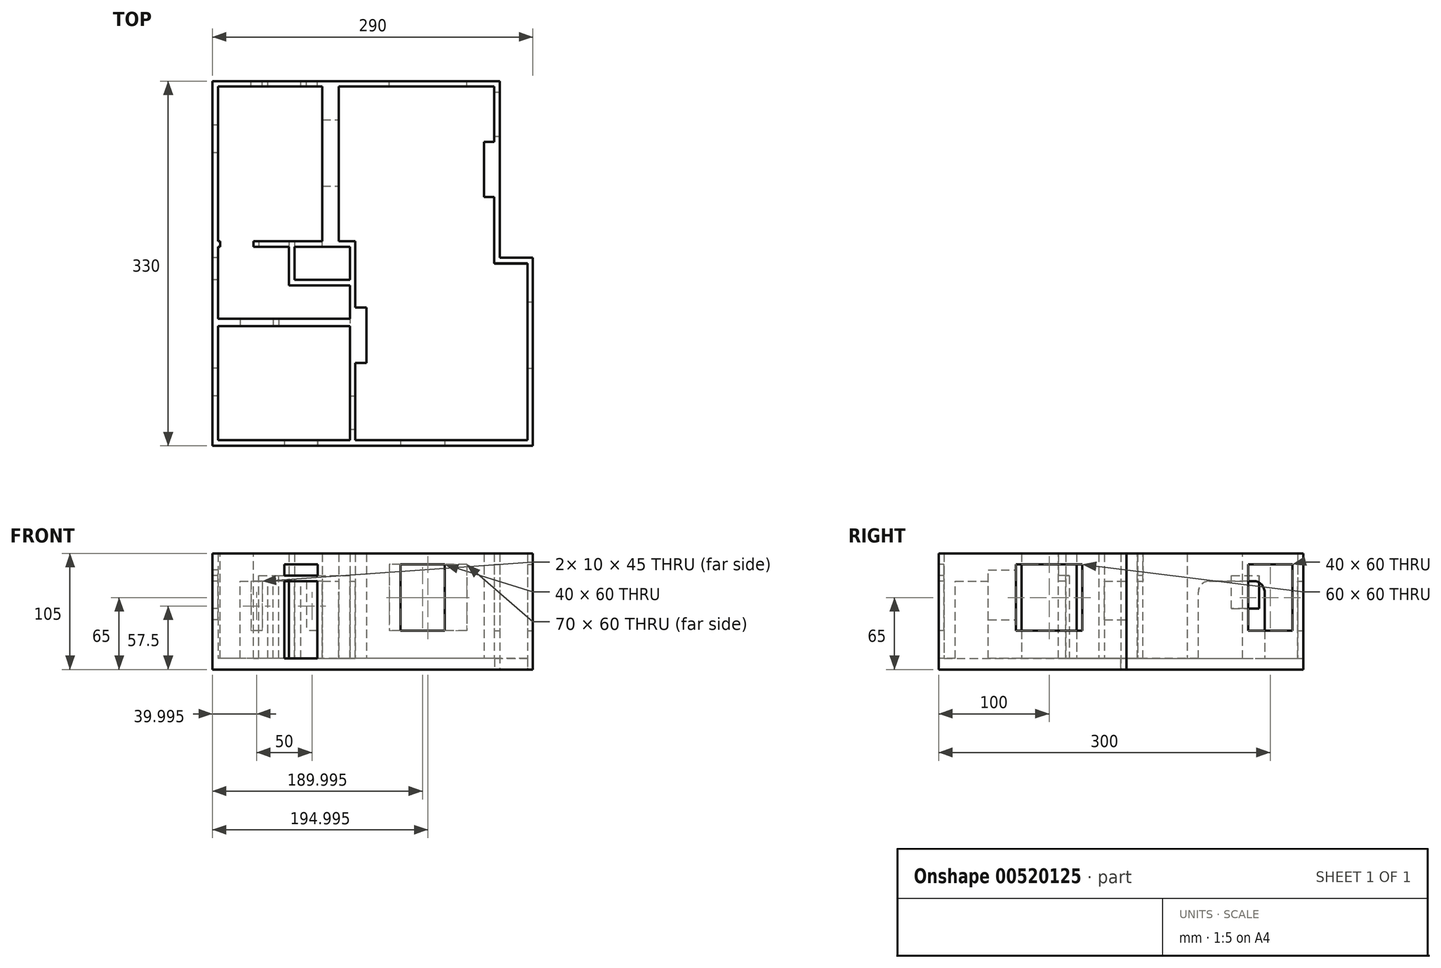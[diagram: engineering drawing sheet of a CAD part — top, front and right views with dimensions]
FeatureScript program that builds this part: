
annotation { "Feature Type Name" : "Feature", "Feature Type Description" : "" }
export const myFeature = defineFeature(function(context is Context, id is Id, definition is map)
    precondition{}
    {
        {
            var Q0;
            Q0=qCreatedBy(makeId("Top.planeOp"),FACE);
            var sketch = newSketch(context, id + "F0", { "sketchPlane" : qUnion([Q0])});
            skLineSegment(sketch, "E0.bottom", {"start": v(-137.2, 155) * mm, "end": v(112.8, 155) * mm});
            skLineSegment(sketch, "E0.top", {"start": v(-137.2, -165) * mm, "end": v(142.8, -165) * mm});
            skLineSegment(sketch, "E0.left", {"start": v(-137.2, 155) * mm, "end": v(-137.2, -165) * mm});
            skLineSegment(sketch, "E0.right", {"start": v(142.8, -5) * mm, "end": v(142.8, -165) * mm});
            skLineSegment(sketch, "E1", {"start": v(112.8, 155) * mm, "end": v(112.8, -5) * mm});
            skLineSegment(sketch, "E2", {"start": v(112.8, -5) * mm, "end": v(142.8, -5) * mm});
            skLineSegment(sketch, "E3.right", {"start": v(112.8, 61.59) * mm, "end": v(112.8, 0.5) * mm});
            skLineSegment(sketch, "E4", {"start": v(117.8, 0) * mm, "end": v(147.8, 0) * mm});
            skLineSegment(sketch, "E5", {"start": v(147.8, 0) * mm, "end": v(147.8, -170) * mm});
            skLineSegment(sketch, "E6", {"start": v(147.8, -170) * mm, "end": v(-142.2, -170) * mm});
            skLineSegment(sketch, "E7", {"start": v(-142.2, -170) * mm, "end": v(-142.2, 160) * mm});
            skLineSegment(sketch, "E8", {"start": v(-142.2, 160) * mm, "end": v(117.8, 160) * mm});
            skLineSegment(sketch, "E9", {"start": v(117.8, 0) * mm, "end": v(117.8, 160) * mm});
            skSolve(sketch);
        }
        {
            var Q0;
            Q0=qCreatedBy(makeId("Top.planeOp"),FACE);
            var sketch = newSketch(context, id + "F1", { "sketchPlane" : qUnion([Q0])});
            skLineSegment(sketch, "E10", {"start": v(-137.23, -165.92) * mm, "end": v(-137.39, 155.26) * mm});
            skLineSegment(sketch, "E11", {"start": v(-137.39, 155.26) * mm, "end": v(113.01, 155.38) * mm});
            skLineSegment(sketch, "E12", {"start": v(144.03, -5.33) * mm, "end": v(143.4, -165.3) * mm});
            skLineSegment(sketch, "E13", {"start": v(143.4, -165.3) * mm, "end": v(-137.23, -165.92) * mm});
            skLineSegment(sketch, "E14", {"start": v(113.01, -5.33) * mm, "end": v(144.03, -5.33) * mm});
            skLineSegment(sketch, "E15", {"start": v(113.01, 155.38) * mm, "end": v(113.01, -5.33) * mm});
            skSolve(sketch);
        }
        {
            var Q0;
            Q0 = qSketchRegion(id + "F1", true);
            extrude(context, id + "F2", {"entities" : qUnion([Q0]), "depth" : 10 * mm, "offsetDistance" : 25 * mm});
        }
        {
            var Q0;
            Q0 = qSketchRegion(id + "F0", true);
            extrude(context, id + "F3", {"entities" : qUnion([Q0]), "operationType" : NewBodyOperationType.ADD, "depth" : 105 * mm, "offsetDistance" : 25 * mm});
        }
        {
            var Q0;
            Q0=makeQuery(id+"F3.boolean.opBoolean","SPLIT",FACE,{"disambiguationData":[TD([makeQuery(id+"F3.opExtrude","SWEPT_FACE",FACE,{"disambiguationData":[OSD([sQuery(id+"F0.wireOp",EDGE,"E0.bottom")])]}),makeQuery(id+"F3.opExtrude","SWEPT_FACE",FACE,{"disambiguationData":[OSD([sQuery(id+"F0.wireOp",EDGE,"E0.top")])]}),makeQuery(id+"F3.opExtrude","SWEPT_FACE",FACE,{"disambiguationData":[OSD([sQuery(id+"F0.wireOp",EDGE,"E0.left")])]}),makeQuery(id+"F3.opExtrude","SWEPT_FACE",FACE,{"disambiguationData":[OSD([sQuery(id+"F0.wireOp",EDGE,"E0.right")])]}),makeQuery(id+"F3.opExtrude","SWEPT_FACE",FACE,{"disambiguationData":[OSD([sQuery(id+"F0.wireOp",EDGE,"E1"),sQuery(id+"F0.wireOp",EDGE,"E3.right")])]}),makeQuery(id+"F3.opExtrude","SWEPT_FACE",FACE,{"disambiguationData":[OSD([sQuery(id+"F0.wireOp",EDGE,"E2")])]})])],"derivedFrom":makeQuery(id+"F2.opExtrude","CAP_FACE",FACE,{"disambiguationData":[OSD([sQuery(id+"F1.wireOp",EDGE,"E10"),sQuery(id+"F1.wireOp",EDGE,"E11"),sQuery(id+"F1.wireOp",EDGE,"AHrGg0TC-f3ZD-vxQt-6p1O-15SQzwXil3k3"),sQuery(id+"F1.wireOp",EDGE,"61pY8PKr-3VqT-7SnW-i4XL-9i2g4O1dyYCC"),sQuery(id+"F1.wireOp",EDGE,"E12"),sQuery(id+"F1.wireOp",EDGE,"E13")])],"isStart":false})});
            var sketch = newSketch(context, id + "F4", { "sketchPlane" : qUnion([Q0])});
            skLineSegment(sketch, "E16", {"start": v(-28.01, 156.19) * mm, "end": v(-27.86, 125) * mm});
            skLineSegment(sketch, "E17", {"start": v(-27.86, 65) * mm, "end": v(-27.86, 15) * mm});
            skLineSegment(sketch, "E18", {"start": v(-42.86, 15) * mm, "end": v(-72.86, 15) * mm});
            skLineSegment(sketch, "E19", {"start": v(-72.86, 9.94) * mm, "end": v(-72.86, -15) * mm});
            skLineSegment(sketch, "E20", {"start": v(-12.86, -15) * mm, "end": v(-12.86, -45) * mm});
            skLineSegment(sketch, "E21", {"start": v(-12.86, -45) * mm, "end": v(-2.86, -45) * mm});
            skLineSegment(sketch, "E22", {"start": v(-2.86, -45) * mm, "end": v(-2.86, -95) * mm});
            skLineSegment(sketch, "E23", {"start": v(-2.86, -95) * mm, "end": v(-12.86, -95) * mm});
            skLineSegment(sketch, "E24", {"start": v(-12.86, -95) * mm, "end": v(-12.86, -166.02) * mm});
            skLineSegment(sketch, "E25", {"start": v(-27.86, 15) * mm, "end": v(-12.86, 15) * mm});
            skLineSegment(sketch, "E26", {"start": v(-12.86, 15) * mm, "end": v(-12.86, -15) * mm});
            skLineSegment(sketch, "E27", {"start": v(113.59, 55) * mm, "end": v(103.59, 55) * mm});
            skLineSegment(sketch, "E28", {"start": v(103.59, 55) * mm, "end": v(103.59, 105) * mm});
            skLineSegment(sketch, "E29", {"start": v(103.59, 105) * mm, "end": v(113.59, 105) * mm});
            skLineSegment(sketch, "E30.bottom", {"start": v(-67.86, 10) * mm, "end": v(-17.86, 10) * mm});
            skLineSegment(sketch, "E30.top", {"start": v(-67.86, -20) * mm, "end": v(-17.86, -20) * mm});
            skLineSegment(sketch, "E30.left", {"start": v(-67.86, 10) * mm, "end": v(-67.86, -20) * mm});
            skLineSegment(sketch, "E30.right", {"start": v(-17.86, 10) * mm, "end": v(-17.86, -20) * mm});
            skLineSegment(sketch, "E31", {"start": v(-17.93, -15) * mm, "end": v(-17.93, -20) * mm});
            skLineSegment(sketch, "E32", {"start": v(-17.86, -166.02) * mm, "end": v(-12.86, -166.02) * mm});
            skLineSegment(sketch, "E33", {"start": v(-42.86, 15) * mm, "end": v(-42.86, 55.12) * mm});
            skPoint(sketch, "E33.startSnap0", {"position": v(-42.86, 10) * mm});
            skLineSegment(sketch, "E34", {"start": v(-42.86, 156.12) * mm, "end": v(-42.86, 115.12) * mm});
            skLineSegment(sketch, "E35", {"start": v(113.59, 105) * mm, "end": v(113.59, 55) * mm});
            skLineSegment(sketch, "E36", {"start": v(-42.86, 115.12) * mm, "end": v(-42.86, 55.12) * mm});
            skLineSegment(sketch, "E37", {"start": v(-27.86, 125) * mm, "end": v(-27.86, 65) * mm});
            skLineSegment(sketch, "E38", {"start": v(-17.91, -55) * mm, "end": v(-139.35, -55.05) * mm});
            skLineSegment(sketch, "E39", {"start": v(-139.35, -55.05) * mm, "end": v(-139.34, -61.75) * mm});
            skLineSegment(sketch, "E40", {"start": v(-139.34, -61.75) * mm, "end": v(-17.9, -61.75) * mm});
            skLineSegment(sketch, "E41.trimOffspring", {"start": v(-17.9, -61.75) * mm, "end": v(-17.86, -166.02) * mm});
            skLineSegment(sketch, "E42", {"start": v(-72.86, -15) * mm, "end": v(-72.86, -25) * mm});
            skLineSegment(sketch, "E43", {"start": v(-72.86, -25) * mm, "end": v(-17.93, -25) * mm});
            skLineSegment(sketch, "E44.trimOffspring", {"start": v(-17.93, -25) * mm, "end": v(-17.91, -55) * mm});
            skLineSegment(sketch, "E45", {"start": v(-72.86, 15) * mm, "end": v(-139.22, 15) * mm});
            skLineSegment(sketch, "E46", {"start": v(-139.22, 15) * mm, "end": v(-139.22, 9.94) * mm});
            skLineSegment(sketch, "E47", {"start": v(-139.22, 9.94) * mm, "end": v(-72.86, 9.94) * mm});
            skLineSegment(sketch, "E48", {"start": v(-42.86, 156.12) * mm, "end": v(-28.01, 156.19) * mm});
            skPoint(sketch, "E49.orphan", {"position": v(-28.05, 165) * mm});
            skPoint(sketch, "E50.end.orphan", {"position": v(-28.05, 158.08) * mm});
            skSolve(sketch);
        }
        {
            var Q0;
            Q0 = qSketchRegion(id + "F4", true);
            extrude(context, id + "F5", {"entities" : qUnion([Q0]), "operationType" : NewBodyOperationType.ADD, "depth" : 95 * mm, "offsetDistance" : 25 * mm});
        }
        {
            var Q0;
            Q0=makeQuery(id+"F3.opExtrude","SWEPT_FACE",FACE,{"disambiguationData":[OSD([sQuery(id+"F0.wireOp",EDGE,"E5")])]});
            var sketch = newSketch(context, id + "F6", { "sketchPlane" : qUnion([Q0])});
            skLineSegment(sketch, "E51.bottom", {"start": v(-100, 95) * mm, "end": v(-40, 95) * mm});
            skLineSegment(sketch, "E51.top", {"start": v(-100, 35) * mm, "end": v(-40, 35) * mm});
            skLineSegment(sketch, "E51.left", {"start": v(-100, 95) * mm, "end": v(-100, 35) * mm});
            skLineSegment(sketch, "E51.right", {"start": v(-40, 95) * mm, "end": v(-40, 35) * mm});
            skSolve(sketch);
        }
        {
            var Q0;
            Q0=makeQuery(id+"F6.imprint","IMPRINT",FACE,{"disambiguationData":[TD([[makeQuery(id+"F6.imprint","IMPRINT",EDGE,{"derivedFrom":sQuery(id+"F6.wireOp",EDGE,"E51.bottom")}),-1.0]])]});
            extrude(context, id + "F7", {"entities" : qUnion([Q0]), "operationType" : NewBodyOperationType.REMOVE, "oppositeDirection" : true, "depth" : 10 * mm, "offsetDistance" : 25 * mm});
        }
        {
            var Q0;
            Q0=makeQuery(id+"F3.opExtrude","SWEPT_FACE",FACE,{"disambiguationData":[OSD([sQuery(id+"F0.wireOp",EDGE,"E9")])]});
            var sketch = newSketch(context, id + "F8", { "sketchPlane" : qUnion([Q0])});
            skLineSegment(sketch, "E52.bottom", {"start": v(110, 95) * mm, "end": v(150, 95) * mm});
            skLineSegment(sketch, "E52.top", {"start": v(110, 35) * mm, "end": v(150, 35) * mm});
            skLineSegment(sketch, "E52.left", {"start": v(110, 95) * mm, "end": v(110, 35) * mm});
            skLineSegment(sketch, "E52.right", {"start": v(150, 95) * mm, "end": v(150, 35) * mm});
            skSolve(sketch);
        }
        {
            var Q0;
            Q0 = qSketchRegion(id + "F8", true);
            extrude(context, id + "F9", {"entities" : qUnion([Q0]), "operationType" : NewBodyOperationType.REMOVE, "oppositeDirection" : true, "depth" : 10 * mm, "offsetDistance" : 25 * mm});
        }
        {
            var Q0;
            Q0=makeQuery(id+"F3.opExtrude","SWEPT_FACE",FACE,{"disambiguationData":[OSD([sQuery(id+"F0.wireOp",EDGE,"E8")])]});
            var sketch = newSketch(context, id + "F10", { "sketchPlane" : qUnion([Q0])});
            skLineSegment(sketch, "E53.bottom", {"start": v(-87.8, 95) * mm, "end": v(-17.8, 95) * mm});
            skLineSegment(sketch, "E53.top", {"start": v(-87.8, 35) * mm, "end": v(-17.8, 35) * mm});
            skLineSegment(sketch, "E53.left", {"start": v(-87.8, 95) * mm, "end": v(-87.8, 35) * mm});
            skLineSegment(sketch, "E53.right", {"start": v(-17.8, 95) * mm, "end": v(-17.8, 35) * mm});
            skLineSegment(sketch, "E54.bottom", {"start": v(97.2, 80) * mm, "end": v(107.2, 80) * mm});
            skLineSegment(sketch, "E54.top", {"start": v(97.2, 35) * mm, "end": v(107.2, 35) * mm});
            skLineSegment(sketch, "E54.left", {"start": v(97.2, 80) * mm, "end": v(97.2, 35) * mm});
            skLineSegment(sketch, "E54.right", {"start": v(107.2, 80) * mm, "end": v(107.2, 35) * mm});
            skLineSegment(sketch, "E55.bottom", {"start": v(47.2, 80) * mm, "end": v(57.2, 80) * mm});
            skLineSegment(sketch, "E55.top", {"start": v(47.2, 35) * mm, "end": v(57.2, 35) * mm});
            skLineSegment(sketch, "E55.left", {"start": v(47.2, 80) * mm, "end": v(47.2, 35) * mm});
            skLineSegment(sketch, "E55.right", {"start": v(57.2, 80) * mm, "end": v(57.2, 35) * mm});
            skLineSegment(sketch, "E56.bottom", {"start": v(62.2, 10) * mm, "end": v(92.2, 10) * mm});
            skLineSegment(sketch, "E56.top", {"start": v(62.2, 80) * mm, "end": v(92.2, 80) * mm});
            skLineSegment(sketch, "E56.left", {"start": v(62.2, 10) * mm, "end": v(62.2, 80) * mm});
            skLineSegment(sketch, "E56.right", {"start": v(92.2, 10) * mm, "end": v(92.2, 80) * mm});
            skSolve(sketch);
        }
        {
            var Q0;
            Q0 = qSketchRegion(id + "F10", true);
            extrude(context, id + "F11", {"entities" : qUnion([Q0]), "operationType" : NewBodyOperationType.REMOVE, "oppositeDirection" : true, "depth" : 10 * mm, "offsetDistance" : 25 * mm});
        }
        {
            var Q0;
            Q0=makeQuery(id+"F3.opExtrude","SWEPT_FACE",FACE,{"disambiguationData":[OSD([sQuery(id+"F0.wireOp",EDGE,"E7")])]});
            var sketch = newSketch(context, id + "F12", { "sketchPlane" : qUnion([Q0])});
            skLineSegment(sketch, "E57.bottom", {"start": v(-120, 85) * mm, "end": v(-95, 85) * mm});
            skLineSegment(sketch, "E57.top", {"start": v(-120, 55) * mm, "end": v(-95, 55) * mm});
            skLineSegment(sketch, "E57.left", {"start": v(-120, 85) * mm, "end": v(-120, 55) * mm});
            skLineSegment(sketch, "E57.right", {"start": v(-95, 85) * mm, "end": v(-95, 55) * mm});
            skLineSegment(sketch, "E58.bottom", {"start": v(0, 80) * mm, "end": v(20, 80) * mm});
            skLineSegment(sketch, "E58.top", {"start": v(0, 45) * mm, "end": v(20, 45) * mm});
            skLineSegment(sketch, "E58.left", {"start": v(0, 80) * mm, "end": v(0, 45) * mm});
            skLineSegment(sketch, "E58.right", {"start": v(20, 80) * mm, "end": v(20, 45) * mm});
            skLineSegment(sketch, "E59.bottom", {"start": v(100, 90) * mm, "end": v(125, 90) * mm});
            skLineSegment(sketch, "E59.top", {"start": v(100, 45) * mm, "end": v(125, 45) * mm});
            skLineSegment(sketch, "E59.left", {"start": v(100, 90) * mm, "end": v(100, 45) * mm});
            skLineSegment(sketch, "E59.right", {"start": v(125, 90) * mm, "end": v(125, 45) * mm});
            skSolve(sketch);
        }
        {
            var Q0;
            Q0 = qSketchRegion(id + "F12", true);
            extrude(context, id + "F13", {"entities" : qUnion([Q0]), "operationType" : NewBodyOperationType.REMOVE, "oppositeDirection" : true, "depth" : 25 * mm, "offsetDistance" : 25 * mm});
        }
        {
            var Q0;
            Q0=makeQuery(id+"F3.opExtrude","SWEPT_FACE",FACE,{"disambiguationData":[OSD([sQuery(id+"F0.wireOp",EDGE,"E6")])]});
            var sketch = newSketch(context, id + "F14", { "sketchPlane" : qUnion([Q0])});
            skLineSegment(sketch, "E60.bottom", {"start": v(-77.2, 10) * mm, "end": v(-47.2, 10) * mm});
            skLineSegment(sketch, "E60.top", {"start": v(-77.2, 80) * mm, "end": v(-47.2, 80) * mm});
            skLineSegment(sketch, "E60.left", {"start": v(-77.2, 10) * mm, "end": v(-77.2, 80) * mm});
            skLineSegment(sketch, "E60.right", {"start": v(-47.2, 10) * mm, "end": v(-47.2, 80) * mm});
            skLineSegment(sketch, "E61.bottom", {"start": v(27.8, 95) * mm, "end": v(67.8, 95) * mm});
            skLineSegment(sketch, "E61.top", {"start": v(27.8, 35) * mm, "end": v(67.8, 35) * mm});
            skLineSegment(sketch, "E61.left", {"start": v(27.8, 95) * mm, "end": v(27.8, 35) * mm});
            skLineSegment(sketch, "E61.right", {"start": v(67.8, 95) * mm, "end": v(67.8, 35) * mm});
            skLineSegment(sketch, "E62.bottom", {"start": v(-77.07, 95) * mm, "end": v(-47.07, 95) * mm});
            skLineSegment(sketch, "E62.top", {"start": v(-77.07, 85) * mm, "end": v(-47.07, 85) * mm});
            skLineSegment(sketch, "E62.left", {"start": v(-77.07, 95) * mm, "end": v(-77.07, 85) * mm});
            skLineSegment(sketch, "E62.right", {"start": v(-47.07, 95) * mm, "end": v(-47.07, 85) * mm});
            skSolve(sketch);
        }
        {
            var Q0;
            Q0 = qSketchRegion(id + "F14", true);
            extrude(context, id + "F15", {"entities" : qUnion([Q0]), "operationType" : NewBodyOperationType.REMOVE, "oppositeDirection" : true, "depth" : 10 * mm, "offsetDistance" : 25 * mm});
        }
        {
            var Q0;
            Q0=makeQuery(id+"F5.opExtrude","SWEPT_FACE",FACE,{"disambiguationData":[OSD([sQuery(id+"F4.wireOp",EDGE,"E18")])]});
            var sketch = newSketch(context, id + "F16", { "sketchPlane" : qUnion([Q0])});
            skLineSegment(sketch, "E63.bottom", {"start": v(42.86, 10) * mm, "end": v(67.86, 10) * mm});
            skLineSegment(sketch, "E63.top", {"start": v(42.86, 80) * mm, "end": v(67.86, 80) * mm});
            skLineSegment(sketch, "E63.left", {"start": v(42.86, 10) * mm, "end": v(42.86, 80) * mm});
            skLineSegment(sketch, "E63.right", {"start": v(67.86, 10) * mm, "end": v(67.86, 80) * mm});
            skSolve(sketch);
        }
        {
            var Q0;
            Q0 = qSketchRegion(id + "F16", true);
            extrude(context, id + "F17", {"entities" : qUnion([Q0]), "operationType" : NewBodyOperationType.REMOVE, "oppositeDirection" : true, "depth" : 10 * mm, "offsetDistance" : 25 * mm});
        }
        {
            var Q0;
            Q0=makeQuery(id+"F5.opExtrude","SWEPT_FACE",FACE,{"disambiguationData":[OSD([sQuery(id+"F4.wireOp",EDGE,"E24")])]});
            var sketch = newSketch(context, id + "F18", { "sketchPlane" : qUnion([Q0])});
            skLineSegment(sketch, "E64.bottom", {"start": v(-155, 10) * mm, "end": v(-125, 10) * mm});
            skLineSegment(sketch, "E64.top", {"start": v(-155, 80) * mm, "end": v(-125, 80) * mm});
            skLineSegment(sketch, "E64.left", {"start": v(-155, 10) * mm, "end": v(-155, 80) * mm});
            skLineSegment(sketch, "E64.right", {"start": v(-125, 10) * mm, "end": v(-125, 80) * mm});
            skSolve(sketch);
        }
        {
            var Q0;
            Q0 = qSketchRegion(id + "F18", true);
            extrude(context, id + "F19", {"entities" : qUnion([Q0]), "operationType" : NewBodyOperationType.REMOVE, "oppositeDirection" : true, "depth" : 10 * mm, "offsetDistance" : 25 * mm});
        }
        {
            var Q0;
            Q0=makeQuery(id+"F5.opExtrude","SWEPT_FACE",FACE,{"disambiguationData":[OSD([sQuery(id+"F4.wireOp",EDGE,"E17"),sQuery(id+"F4.wireOp",EDGE,"E37")])]});
            var sketch = newSketch(context, id + "F20", { "sketchPlane" : qUnion([Q0])});
            skLineSegment(sketch, "E65.bottom", {"start": v(125, 10) * mm, "end": v(65, 10) * mm});
            skLineSegment(sketch, "E65.top", {"start": v(115, 80) * mm, "end": v(75, 80) * mm});
            skLineSegment(sketch, "E65.left", {"start": v(125, 10) * mm, "end": v(125, 70) * mm});
            skLineSegment(sketch, "E65.right", {"start": v(65, 10) * mm, "end": v(65, 70) * mm});
            skPoint(sketch, "E66.visualSharp", {"position": v(65, 80) * mm});
            skArc(sketch, "E66.filletArc", {"start": v(75, 80) * mm, "mid": v(67.93, 77.07) * mm, "end": v(65, 70) * mm});
            skPoint(sketch, "E67.visualSharp", {"position": v(125, 80) * mm});
            skArc(sketch, "E67.filletArc", {"start": v(125, 70) * mm, "mid": v(122.07, 77.07) * mm, "end": v(115, 80) * mm});
            skSolve(sketch);
        }
        {
            var Q0;
            Q0 = qSketchRegion(id + "F20", true);
            extrude(context, id + "F21", {"entities" : qUnion([Q0]), "operationType" : NewBodyOperationType.REMOVE, "oppositeDirection" : true, "depth" : 15 * mm, "offsetDistance" : 25 * mm});
        }
        {
            var Q0;
            Q0=makeQuery(id+"F5.opExtrude","SWEPT_FACE",FACE,{"disambiguationData":[OSD([sQuery(id+"F4.wireOp",EDGE,"E40")])]});
            var sketch = newSketch(context, id + "F22", { "sketchPlane" : qUnion([Q0])});
            skLineSegment(sketch, "E68.bottom", {"start": v(-117.2, 10) * mm, "end": v(-87.2, 10) * mm});
            skLineSegment(sketch, "E68.top", {"start": v(-117.2, 80) * mm, "end": v(-87.2, 80) * mm});
            skLineSegment(sketch, "E68.left", {"start": v(-117.2, 10) * mm, "end": v(-117.2, 80) * mm});
            skLineSegment(sketch, "E68.right", {"start": v(-87.2, 10) * mm, "end": v(-87.2, 80) * mm});
            skLineSegment(sketch, "E69.bottom", {"start": v(-82.2, 10) * mm, "end": v(-17.9, 10) * mm});
            skLineSegment(sketch, "E69.top", {"start": v(-82.2, 85) * mm, "end": v(-17.9, 85) * mm});
            skLineSegment(sketch, "E69.left", {"start": v(-82.2, 10) * mm, "end": v(-82.2, 85) * mm});
            skLineSegment(sketch, "E69.right", {"start": v(-17.9, 10) * mm, "end": v(-17.9, 85) * mm});
            skSolve(sketch);
        }
        {
            var Q0;
            Q0 = qSketchRegion(id + "F22", true);
            extrude(context, id + "F23", {"entities" : qUnion([Q0]), "operationType" : NewBodyOperationType.REMOVE, "oppositeDirection" : true, "depth" : 10 * mm, "offsetDistance" : 25 * mm});
        }
        {
            var Q0;
            Q0=makeQuery(id+"F5.opExtrude","SWEPT_FACE",FACE,{"disambiguationData":[OSD([sQuery(id+"F4.wireOp",EDGE,"E47")])]});
            var sketch = newSketch(context, id + "F24", { "sketchPlane" : qUnion([Q0])});
            skLineSegment(sketch, "E70.bottom", {"start": v(-135.2, 10) * mm, "end": v(-105.2, 10) * mm});
            skLineSegment(sketch, "E70.top", {"start": v(-135.2, 105) * mm, "end": v(-105.2, 105) * mm});
            skLineSegment(sketch, "E70.left", {"start": v(-135.2, 10) * mm, "end": v(-135.2, 105) * mm});
            skLineSegment(sketch, "E70.right", {"start": v(-105.2, 10) * mm, "end": v(-105.2, 105) * mm});
            skLineSegment(sketch, "E71.bottom", {"start": v(-100.2, 10) * mm, "end": v(-72.86, 10) * mm});
            skLineSegment(sketch, "E71.top", {"start": v(-100.2, 85) * mm, "end": v(-72.86, 85) * mm});
            skLineSegment(sketch, "E71.left", {"start": v(-100.2, 10) * mm, "end": v(-100.2, 85) * mm});
            skLineSegment(sketch, "E71.right", {"start": v(-72.86, 10) * mm, "end": v(-72.86, 85) * mm});
            skSolve(sketch);
        }
        {
            var Q0;
            Q0 = qSketchRegion(id + "F24", true);
            extrude(context, id + "F25", {"entities" : qUnion([Q0]), "operationType" : NewBodyOperationType.REMOVE, "oppositeDirection" : true, "depth" : 10 * mm, "offsetDistance" : 25 * mm});
        }
    });
